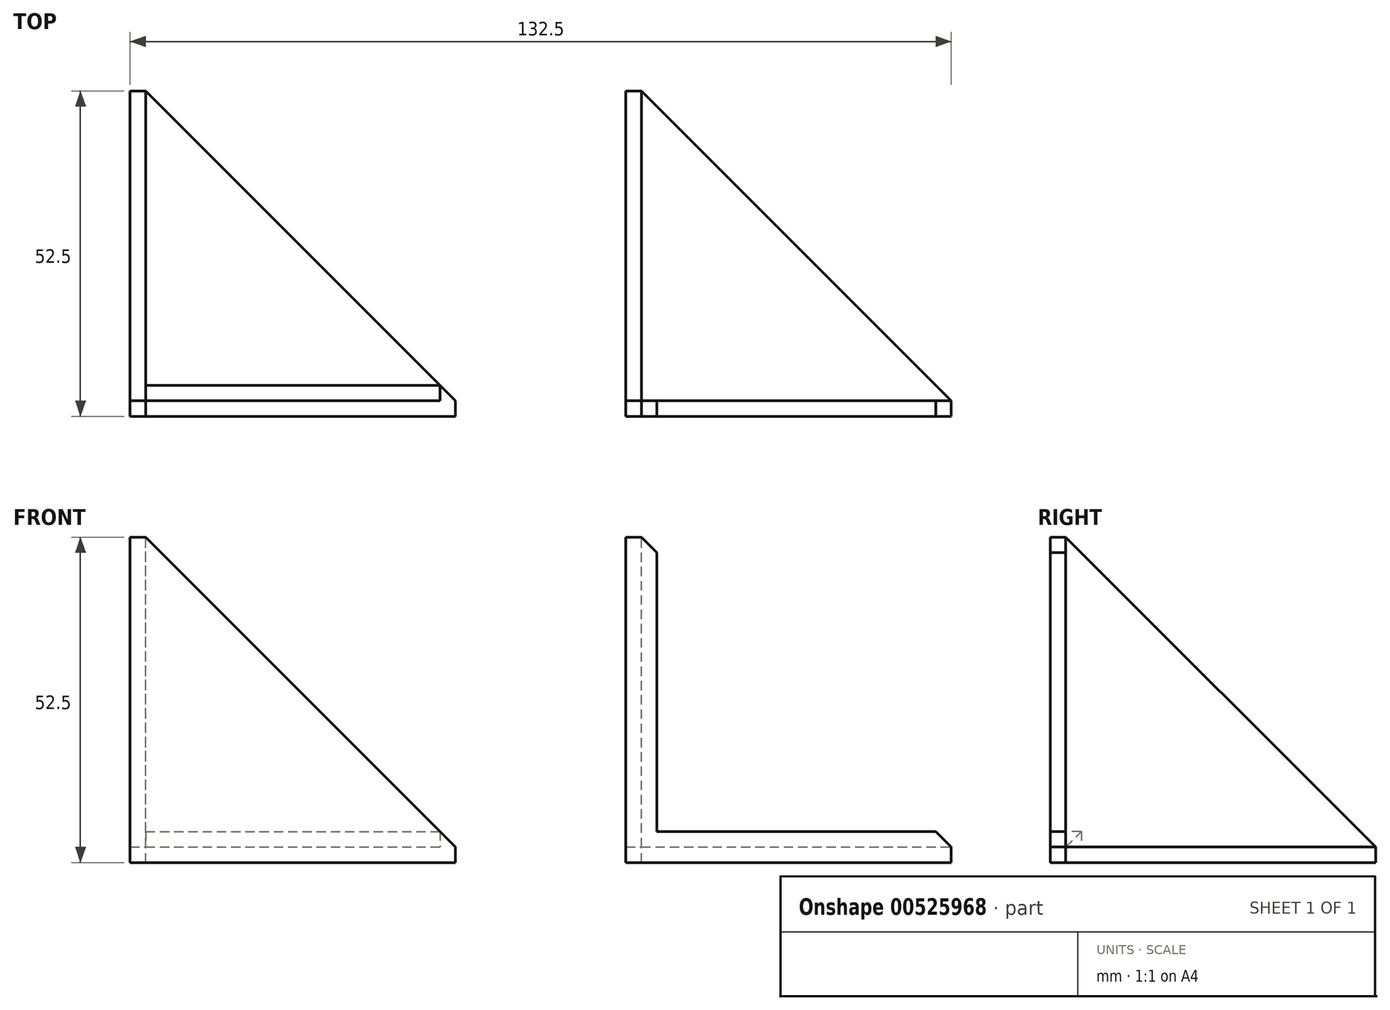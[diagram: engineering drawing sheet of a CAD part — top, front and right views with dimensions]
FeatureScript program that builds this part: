
annotation { "Feature Type Name" : "Feature", "Feature Type Description" : "" }
export const myFeature = defineFeature(function(context is Context, id is Id, definition is map)
    precondition{}
    {
        {
            var Q0;
            Q0=qCreatedBy(makeId("Top.planeOp"),FACE);
            var sketch = newSketch(context, id + "F0", { "sketchPlane" : qUnion([Q0])});
            skLineSegment(sketch, "E0", {"start": v(-23, 26.92) * mm, "end": v(-23, -23.08) * mm});
            skLineSegment(sketch, "E1", {"start": v(-23, -23.08) * mm, "end": v(27, -23.08) * mm});
            skLineSegment(sketch, "E2", {"start": v(27, -23.08) * mm, "end": v(-23, 26.92) * mm});
            skLineSegment(sketch, "E3", {"start": v(-23, -20.58) * mm, "end": v(24.5, -20.58) * mm});
            skSolve(sketch);
        }
        {
            var Q0;
            Q0=makeQuery(id+"F0.imprint","IMPRINT",FACE,{"disambiguationData":[TD([[makeQuery(id+"F0.imprint","IMPRINT",EDGE,{"derivedFrom":sQuery(id+"F0.wireOp",EDGE,"E0")}),1.0]])]});
            var Q1;
            {var subQ0=sQuery(id+"F0.wireOp",EDGE,"E1");Q1=makeQuery(id+"F0.imprint","IMPRINT",FACE,{"disambiguationData":[TD([[makeQuery(id+"F0.imprint","IMPRINT",EDGE,{"derivedFrom":subQ0}),1.0]])]});}
            extrude(context, id + "F1", {"entities" : qUnion([Q0, Q1]), "oppositeDirection" : true, "depth" : 2.5 * mm, "offsetDistance" : 25 * mm});
        }
        {
            var Q0;
            Q0=makeQuery(id+"F1.opExtrude","SWEPT_FACE",FACE,{"disambiguationData":[OSD([sQuery(id+"F0.wireOp",EDGE,"E1")])]});
            var sketch = newSketch(context, id + "F2", { "sketchPlane" : qUnion([Q0])});
            skLineSegment(sketch, "E4", {"start": v(-23, 0) * mm, "end": v(-23, 50) * mm});
            skLineSegment(sketch, "E5", {"start": v(-23, 50) * mm, "end": v(27, 0) * mm});
            skSolve(sketch);
        }
        {
            var Q0;
            Q0 = qSketchRegion(id + "F2", true);
            var Q1;
            Q1=makeQuery(id+"F2.imprint","IMPRINT",FACE,{"disambiguationData":[TD([[makeQuery(id+"F2.imprint","IMPRINT",EDGE,{"derivedFrom":sQuery(id+"F2.wireOp",EDGE,"E4")}),-1.0]])]});
            var Q2;
            {var subQ0=sQuery(id+"F0.wireOp",EDGE,"E1");Q2=makeQuery(id+"F2.imprint","IMPRINT",FACE,{"disambiguationData":[TD([[makeQuery(id+"F2.imprint","IMPRINT",EDGE,{"derivedFrom":makeQuery(id+"F1.opExtrude","CAP_EDGE",EDGE,{"disambiguationData":[OSD([subQ0])],"isStart":true})}),-1.0]])]});}
            extrude(context, id + "F3", {"entities" : qUnion([Q0, Q1, Q2]), "operationType" : NewBodyOperationType.ADD, "depth" : 2.5 * mm, "offsetDistance" : 25 * mm});
        }
        {
            var Q0;
            {var subQ0=sQuery(id+"F0.wireOp",EDGE,"E0");Q0=makeQuery(id+"F3.boolean.opBoolean","MERGE",FACE,{"derivedFrom":[makeQuery(id+"F1.opExtrude","SWEPT_FACE",FACE,{"disambiguationData":[OSD([subQ0])]}),makeQuery(id+"F3.opExtrude","SWEPT_FACE",FACE,{"disambiguationData":[OSD([subQ0,sQuery(id+"F0.wireOp",EDGE,"E1"),sQuery(id+"F2.wireOp",EDGE,"E4")])]})]});}
            var sketch = newSketch(context, id + "F4", { "sketchPlane" : qUnion([Q0])});
            skLineSegment(sketch, "E6", {"start": v(-26.92, 0) * mm, "end": v(23.08, 50) * mm});
            skSolve(sketch);
        }
        {
            var Q0;
            Q0 = qSketchRegion(id + "F4", true);
            var Q1;
            Q1=makeQuery(id+"F4.imprint","IMPRINT",FACE,{"disambiguationData":[TD([[makeQuery(id+"F4.imprint","IMPRINT",EDGE,{"derivedFrom":sQuery(id+"F4.wireOp",EDGE,"E6")}),-1.0]])]});
            var Q2;
            {var subQ2=sQuery(id+"F0.wireOp",EDGE,"E0");Q2=makeQuery(id+"F4.imprint","IMPRINT",FACE,{"disambiguationData":[TD([[makeQuery(id+"F4.imprint","IMPRINT",EDGE,{"derivedFrom":makeQuery(id+"F1.opExtrude","CAP_EDGE",EDGE,{"disambiguationData":[OSD([subQ2])],"isStart":true})}),-1.0]])]});}
            extrude(context, id + "F5", {"entities" : qUnion([Q0, Q1, Q2]), "operationType" : NewBodyOperationType.ADD, "depth" : 2.5 * mm, "offsetDistance" : 25 * mm});
        }
        {
            var Q0;
            Q0=makeQuery(id+"F1.opExtrude","SWEPT_BODY",BODY,{"disambiguationData":[OSD([sQuery(id+"F0.wireOp",EDGE,"E0"),sQuery(id+"F0.wireOp",EDGE,"E1"),sQuery(id+"F0.wireOp",EDGE,"E2")])]});
            transform(context, id + "F6", {"entities" : qUnion([Q0]), "transformType" : TransformType.TRANSLATION_3D, "dx" : 80 * mm, "dy" : 0 * mm, "dz" : 0 * mm, "makeCopy" : true});
        }
        {
            var Q0;
            {var subQ0=sQuery(id+"F2.wireOp",EDGE,"E4");var subQ1=sQuery(id+"F0.wireOp",EDGE,"E1");var subQ2=sQuery(id+"F0.wireOp",EDGE,"E0");Q0=makeQuery(id+"F6.opPattern","COPY",FACE,{"derivedFrom":makeQuery(id+"F5.boolean.opBoolean","MERGE",FACE,{"derivedFrom":[makeQuery(id+"F3.opExtrude","CAP_FACE",FACE,{"disambiguationData":[OSD([subQ2,subQ1,sQuery(id+"F0.wireOp",EDGE,"E2"),subQ0,sQuery(id+"F2.wireOp",EDGE,"E5")])],"isStart":false}),makeQuery(id+"F5.opExtrude","SWEPT_FACE",FACE,{"disambiguationData":[OSD([subQ2,subQ1,subQ0])]})]}),"instanceName":"1"});}
            var sketch = newSketch(context, id + "F7", { "sketchPlane" : qUnion([Q0])});
            skLineSegment(sketch, "E7", {"start": v(57, 50) * mm, "end": v(57, 0) * mm});
            skLineSegment(sketch, "E8", {"start": v(57, 0) * mm, "end": v(107, 0) * mm});
            skLineSegment(sketch, "E9", {"start": v(59.5, 0) * mm, "end": v(59.5, 47.5) * mm});
            skLineSegment(sketch, "E10", {"start": v(57, 2.5) * mm, "end": v(104.5, 2.5) * mm});
            skLineSegment(sketch, "E11.bottom", {"start": v(57, 0) * mm, "end": v(59.5, 0) * mm});
            skLineSegment(sketch, "E11.top", {"start": v(57, 2.5) * mm, "end": v(59.5, 2.5) * mm});
            skLineSegment(sketch, "E11.left", {"start": v(57, 0) * mm, "end": v(57, 2.5) * mm});
            skLineSegment(sketch, "E11.right", {"start": v(59.5, 0) * mm, "end": v(59.5, 2.5) * mm});
            skSolve(sketch);
        }
        {
            var Q0;
            {var subQ0=sQuery(id+"F7.wireOp",EDGE,"E9");Q0=makeQuery(id+"F7.imprint","IMPRINT",FACE,{"disambiguationData":[TD([[makeQuery(id+"F7.imprint","IMPRINT",EDGE,{"derivedFrom":subQ0}),-1.0]])]});}
            extrude(context, id + "F8", {"entities" : qUnion([Q0]), "operationType" : NewBodyOperationType.REMOVE, "oppositeDirection" : true, "depth" : 2.5 * mm, "offsetDistance" : 25 * mm});
        }
        {
            var Q0;
            {var subQ0=sQuery(id+"F0.wireOp",EDGE,"E1");Q0=makeQuery(id+"F0.imprint","IMPRINT",FACE,{"disambiguationData":[TD([[makeQuery(id+"F0.imprint","IMPRINT",EDGE,{"derivedFrom":subQ0}),1.0]])]});}
            extrude(context, id + "F9", {"entities" : qUnion([Q0]), "operationType" : NewBodyOperationType.ADD, "depth" : 2.5 * mm, "offsetDistance" : 25 * mm});
        }
        {
            var Q0;
            Q0=makeQuery(id+"F9.opExtrude","SWEPT_FACE",FACE,{"disambiguationData":[OSD([sQuery(id+"F0.wireOp",EDGE,"E1")])]});
            extrude(context, id + "F10", {"entities" : qUnion([Q0]), "operationType" : NewBodyOperationType.REMOVE, "oppositeDirection" : true, "depth" : 2.5 * mm, "offsetDistance" : 25 * mm});
        }
    });
